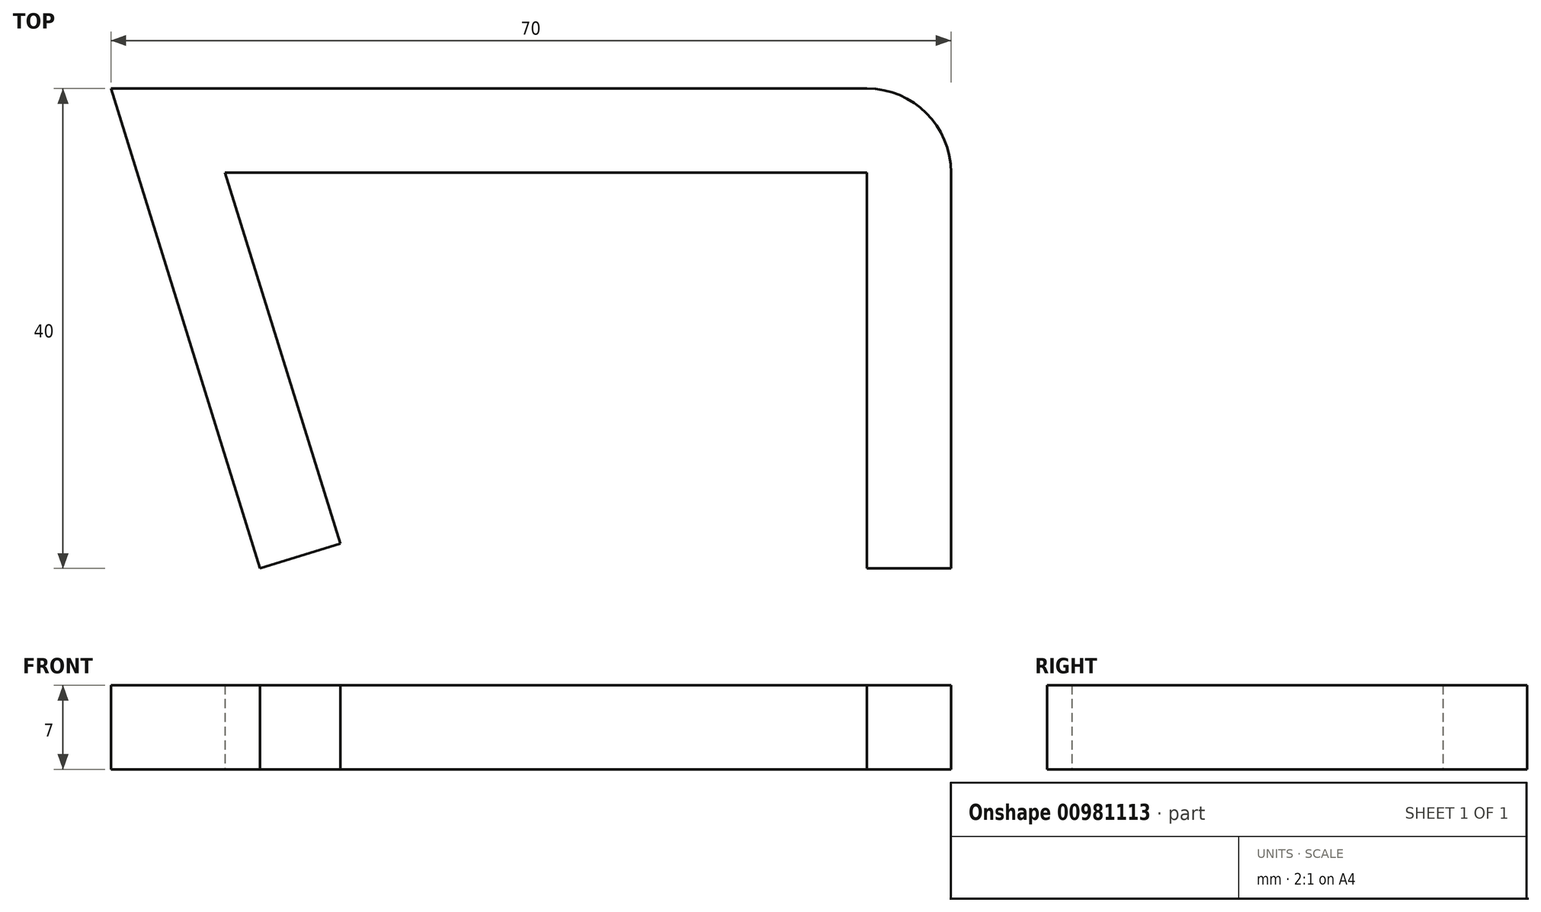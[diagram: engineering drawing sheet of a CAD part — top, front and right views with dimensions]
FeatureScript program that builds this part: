
annotation { "Feature Type Name" : "Feature", "Feature Type Description" : "" }
export const myFeature = defineFeature(function(context is Context, id is Id, definition is map)
    precondition{}
    {
        {
            var Q0;
            Q0=qCreatedBy(makeId("Top.planeOp"),FACE);
            var sketch = newSketch(context, id + "F0", { "sketchPlane" : qUnion([Q0])});
            skLineSegment(sketch, "E0.bottom", {"start": v(5.23, -16.32) * mm, "end": v(12.23, -16.32) * mm});
            skLineSegment(sketch, "E0.top", {"start": v(-57.77, 23.68) * mm, "end": v(5.23, 23.68) * mm});
            skLineSegment(sketch, "E0.right", {"start": v(12.23, -16.32) * mm, "end": v(12.23, 16.68) * mm});
            skPoint(sketch, "E1.visualSharp", {"position": v(12.23, 23.68) * mm});
            skArc(sketch, "E1.filletArc", {"start": v(12.23, 16.68) * mm, "mid": v(10.18, 21.63) * mm, "end": v(5.23, 23.68) * mm});
            skLineSegment(sketch, "E2", {"start": v(-57.77, 23.68) * mm, "end": v(-45.35, -16.32) * mm});
            skLineSegment(sketch, "E3", {"start": v(-45.35, -16.32) * mm, "end": v(-38.66, -14.24) * mm});
            skLineSegment(sketch, "E4", {"start": v(-38.66, -14.24) * mm, "end": v(-48.26, 16.68) * mm});
            skPoint(sketch, "E5", {"position": v(5.23, -16.32) * mm});
            skLineSegment(sketch, "E6", {"start": v(5.23, -16.32) * mm, "end": v(5.23, 16.68) * mm});
            skLineSegment(sketch, "E7", {"start": v(-48.26, 16.68) * mm, "end": v(5.23, 16.68) * mm});
            skSolve(sketch);
        }
        {
            var Q0;
            Q0 = qSketchRegion(id + "F0", true);
            extrude(context, id + "F1", {"entities" : qUnion([Q0]), "depth" : 7 * mm, "offsetDistance" : 25 * mm});
        }
    });
